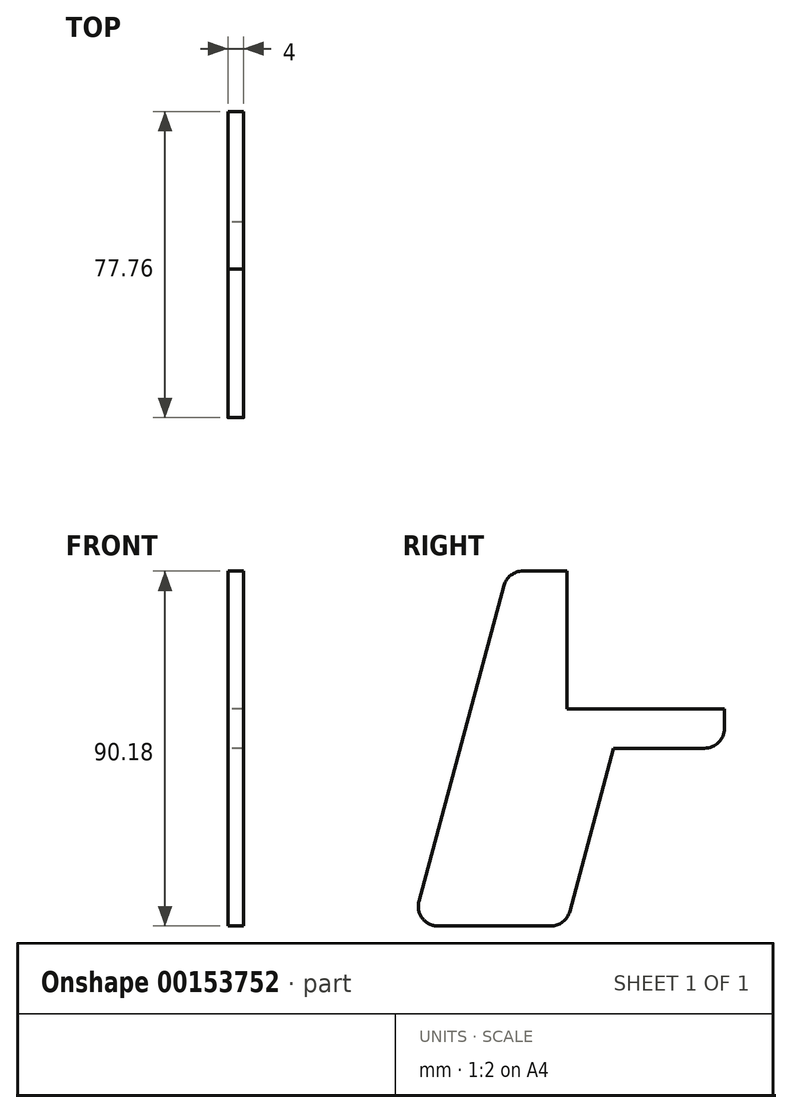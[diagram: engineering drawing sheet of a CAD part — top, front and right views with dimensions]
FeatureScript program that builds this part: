
annotation { "Feature Type Name" : "Feature", "Feature Type Description" : "" }
export const myFeature = defineFeature(function(context is Context, id is Id, definition is map)
    precondition{}
    {
        {
            var Q0;
            Q0=qCreatedBy(makeId("Right.planeOp"),FACE);
            var sketch = newSketch(context, id + "F0", { "sketchPlane" : qUnion([Q0])});
            skLineSegment(sketch, "E0", {"start": v(0, 0) * mm, "end": v(0, 35) * mm});
            skLineSegment(sketch, "E1", {"start": v(0, 0) * mm, "end": v(40, 0) * mm});
            skLineSegment(sketch, "E2", {"start": v(0, 35) * mm, "end": v(-11.17, 35) * mm});
            skLineSegment(sketch, "E3", {"start": v(40, 0) * mm, "end": v(40, -5) * mm});
            skLineSegment(sketch, "E4", {"start": v(35, -10) * mm, "end": v(11.9, -10) * mm});
            skLineSegment(sketch, "E5", {"start": v(11.9, -10) * mm, "end": v(0.72, -51.48) * mm});
            skPoint(sketch, "E6.orphan", {"position": v(0, -10) * mm});
            skLineSegment(sketch, "E7", {"start": v(-16, 31.3) * mm, "end": v(-37.59, -48.88) * mm});
            skLineSegment(sketch, "E8", {"start": v(-32.76, -55.18) * mm, "end": v(-4.1, -55.18) * mm});
            skPoint(sketch, "E9.visualSharp", {"position": v(40, -10) * mm});
            skArc(sketch, "E9.filletArc", {"start": v(35, -10) * mm, "mid": v(38.54, -8.54) * mm, "end": v(40, -5) * mm});
            skArc(sketch, "E10.filletArc", {"start": v(-4.1, -55.18) * mm, "mid": v(-1.06, -54.14) * mm, "end": v(0.72, -51.48) * mm});
            skArc(sketch, "E11.filletArc", {"start": v(-37.59, -48.88) * mm, "mid": v(-36.73, -53.22) * mm, "end": v(-32.76, -55.18) * mm});
            skPoint(sketch, "E12.visualSharp", {"position": v(-15, 35) * mm});
            skArc(sketch, "E12.filletArc", {"start": v(-11.17, 35) * mm, "mid": v(-14.2, 33.97) * mm, "end": v(-16, 31.3) * mm});
            skSolve(sketch);
        }
        {
            var Q0;
            Q0=makeQuery(id+"F0.imprint","IMPRINT",FACE,{"disambiguationData":[TD([[makeQuery(id+"F0.imprint","IMPRINT",EDGE,{"derivedFrom":sQuery(id+"F0.wireOp",EDGE,"E0")}),1.0]])]});
            extrude(context, id + "F1", {"entities" : qUnion([Q0]), "depth" : 4 * mm});
        }
    });
